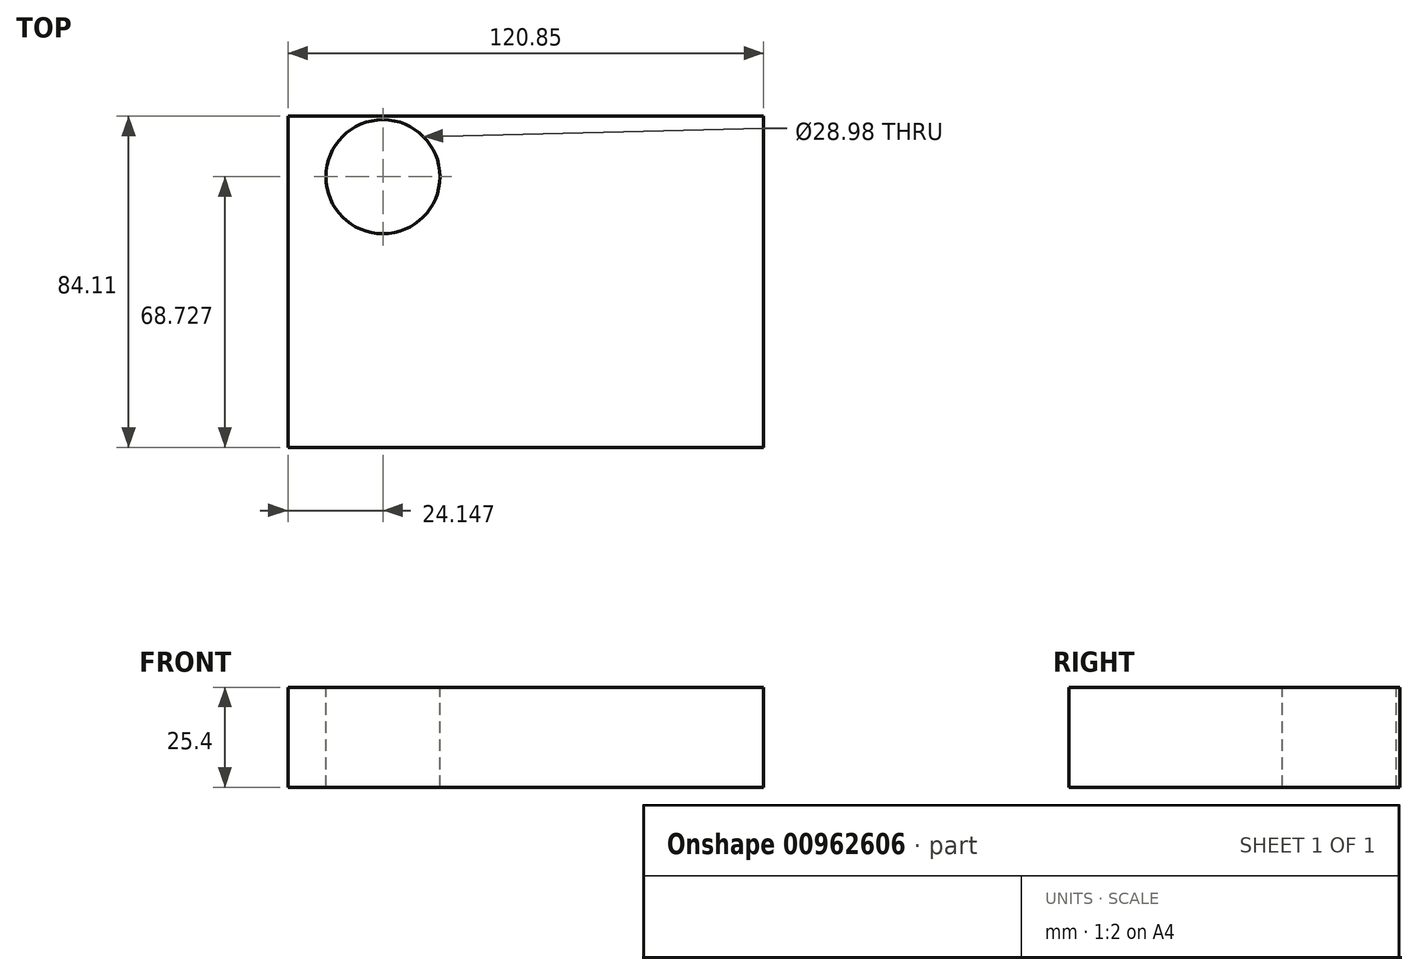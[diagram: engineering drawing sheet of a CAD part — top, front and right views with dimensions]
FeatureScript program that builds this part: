
annotation { "Feature Type Name" : "Feature", "Feature Type Description" : "" }
export const myFeature = defineFeature(function(context is Context, id is Id, definition is map)
    precondition{}
    {
        {
            var Q0;
            Q0=qCreatedBy(makeId("Top.planeOp"),FACE);
            var sketch = newSketch(context, id + "F0", { "sketchPlane" : qUnion([Q0])});
            skLineSegment(sketch, "E0.bottom", {"start": v(-56.8, 38.77) * mm, "end": v(64.05, 38.77) * mm});
            skLineSegment(sketch, "E0.top", {"start": v(-56.8, -45.34) * mm, "end": v(64.05, -45.34) * mm});
            skLineSegment(sketch, "E0.left", {"start": v(-56.8, 38.77) * mm, "end": v(-56.8, -45.34) * mm});
            skLineSegment(sketch, "E0.right", {"start": v(64.05, 38.77) * mm, "end": v(64.05, -45.34) * mm});
            skSolve(sketch);
        }
        {
            var Q0;
            Q0=makeQuery(id+"F0.imprint","IMPRINT",FACE,{"disambiguationData":[TD([[makeQuery(id+"F0.imprint","IMPRINT",EDGE,{"derivedFrom":sQuery(id+"F0.wireOp",EDGE,"E0.bottom")}),-1.0]])]});
            extrude(context, id + "F1", {"entities" : qUnion([Q0]), "depth" : 25.4 * mm, "offsetDistance" : 25.4 * mm});
        }
        {
            var Q0;
            Q0=makeQuery(id+"F1.opExtrude","CAP_FACE",FACE,{"disambiguationData":[OSD([sQuery(id+"F0.wireOp",EDGE,"E0.bottom"),sQuery(id+"F0.wireOp",EDGE,"E0.top"),sQuery(id+"F0.wireOp",EDGE,"E0.left"),sQuery(id+"F0.wireOp",EDGE,"E0.right")])],"isStart":false});
            var sketch = newSketch(context, id + "F2", { "sketchPlane" : qUnion([Q0])});
            skSolve(sketch);
        }
        {
            var Q0;
            Q0=makeQuery(id+"F2.imprint","IMPRINT",FACE,{"disambiguationData":[TD([[makeQuery(id+"F2.imprint","IMPRINT",EDGE,{"derivedFrom":makeQuery(id+"F1.opExtrude","CAP_EDGE",EDGE,{"disambiguationData":[OSD([sQuery(id+"F0.wireOp",EDGE,"E0.bottom")])],"isStart":false})}),-1.0]])]});
            var sketch = newSketch(context, id + "F3", { "sketchPlane" : qUnion([Q0])});
            skCircle(sketch, "E1", {"center": v(-32.65, 23.39) * mm, "radius": 14.5 * mm});
            skSolve(sketch);
        }
        {
            var Q0;
            Q0=makeQuery(id+"F3.imprint","IMPRINT",FACE,{"disambiguationData":[TD([[makeQuery(id+"F3.imprint","IMPRINT",EDGE,{"derivedFrom":sQuery(id+"F3.wireOp",EDGE,"E1")}),1.0]])]});
            extrude(context, id + "F4", {"entities" : qUnion([Q0]), "operationType" : NewBodyOperationType.REMOVE, "oppositeDirection" : true, "depth" : 115.77 * mm, "offsetDistance" : 25.4 * mm});
        }
    });
